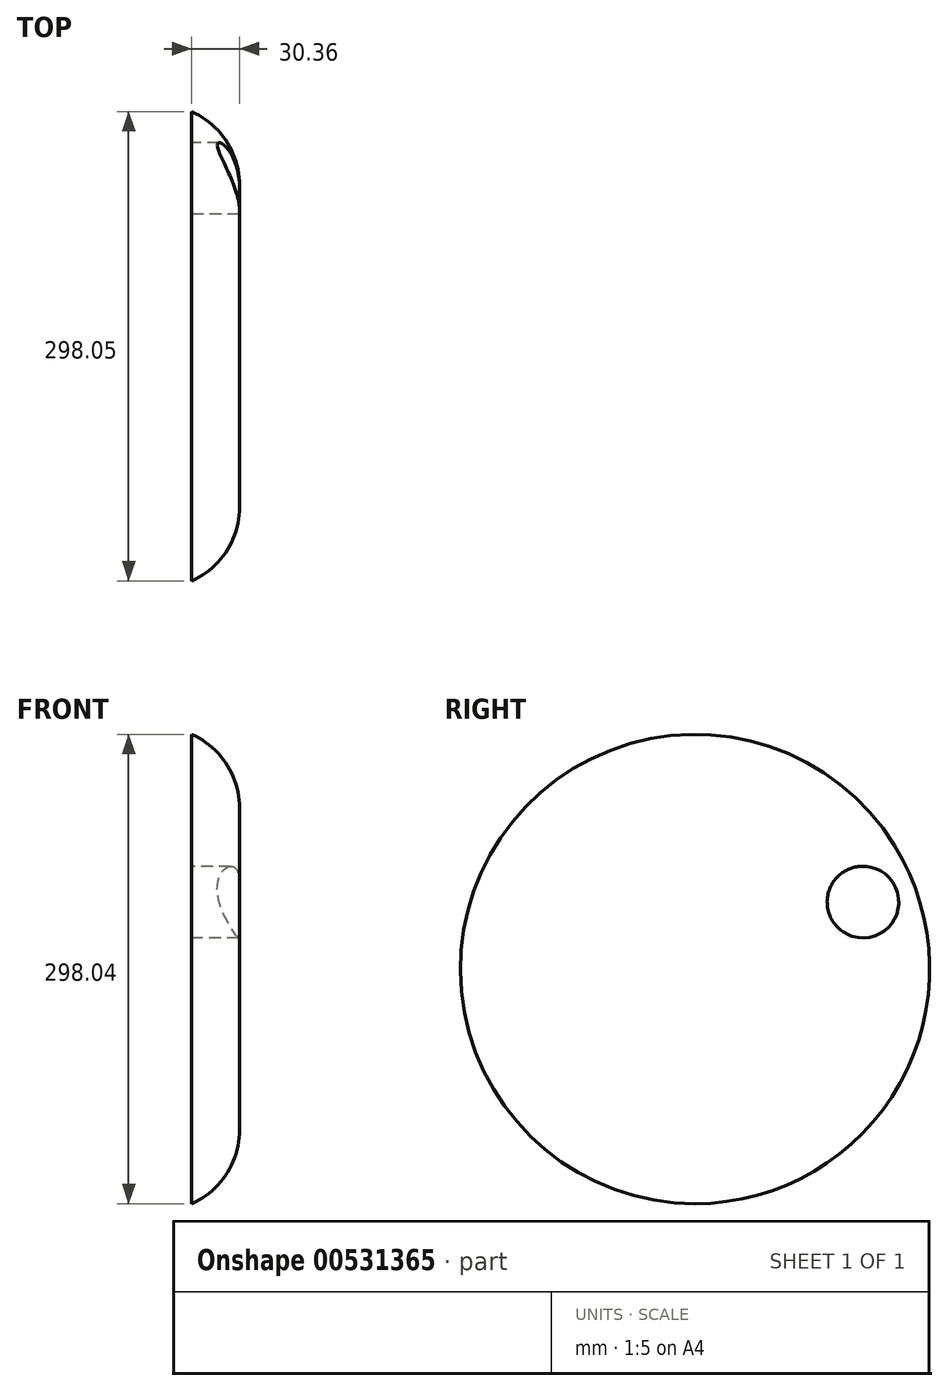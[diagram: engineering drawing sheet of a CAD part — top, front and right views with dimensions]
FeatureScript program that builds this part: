
annotation { "Feature Type Name" : "Feature", "Feature Type Description" : "" }
export const myFeature = defineFeature(function(context is Context, id is Id, definition is map)
    precondition{}
    {
        {
            var Q0;
            Q0=qCreatedBy(makeId("Right.planeOp"),FACE);
            var sketch = newSketch(context, id + "F0", { "sketchPlane" : qUnion([Q0])});
            skCircle(sketch, "E0", {"center": v(15.66, -18.18) * mm, "radius": 149.02 * mm});
            skCircle(sketch, "E1", {"center": v(122.3, 24.37) * mm, "radius": 22.75 * mm});
            skSolve(sketch);
        }
        {
            var Q0;
            Q0=makeQuery(id+"F0.imprint","IMPRINT",FACE,{"disambiguationData":[TD([[makeQuery(id+"F0.imprint","IMPRINT",EDGE,{"derivedFrom":sQuery(id+"F0.wireOp",EDGE,"E0")}),1.0]])]});
            extrude(context, id + "F1", {"entities" : qUnion([Q0]), "depth" : 30.36 * mm, "offsetDistance" : 25.4 * mm});
        }
        {
            var Q0;
            Q0=makeQuery(id+"F1.opExtrude","CAP_EDGE",EDGE,{"disambiguationData":[OSD([sQuery(id+"F0.wireOp",EDGE,"E0")])],"isStart":false});
            fillet(context, id + "F2", {"entities" : qUnion([Q0]), "radius" : 51.28 * mm, "tangentPropagation" : true, "allowEdgeOverflow" : false});
        }
    });
